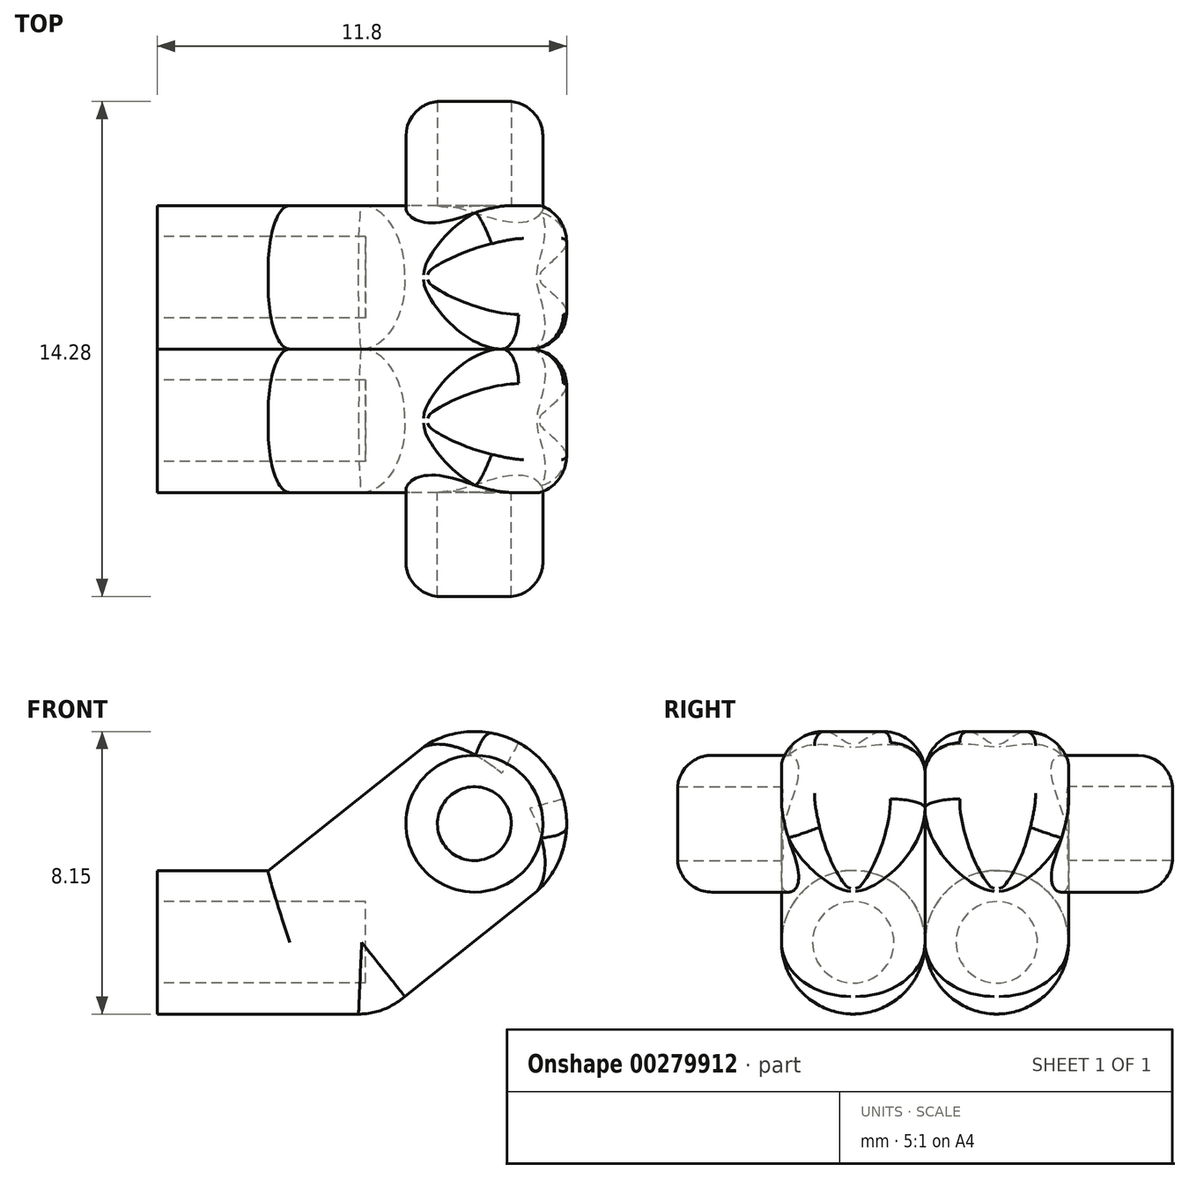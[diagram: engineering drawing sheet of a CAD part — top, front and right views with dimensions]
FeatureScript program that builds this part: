
annotation { "Feature Type Name" : "Feature", "Feature Type Description" : "" }
export const myFeature = defineFeature(function(context is Context, id is Id, definition is map)
    precondition{}
    {
        {
            var Q0;
            Q0=qCreatedBy(makeId("Right.planeOp"),FACE);
            var sketch = newSketch(context, id + "F0", { "sketchPlane" : qUnion([Q0])});
            skLineSegment(sketch, "E0.bottom", {"start": v(2.07, 2.07) * mm, "end": v(-2.07, 2.07) * mm});
            skLineSegment(sketch, "E0.top", {"start": v(2.07, -2.07) * mm, "end": v(-2.07, -2.07) * mm});
            skLineSegment(sketch, "E0.left", {"start": v(2.07, 2.07) * mm, "end": v(2.07, -2.07) * mm});
            skLineSegment(sketch, "E0.right", {"start": v(-2.07, 2.07) * mm, "end": v(-2.07, -2.07) * mm});
            skPoint(sketch, "E0.middle", {"position": v(0, 0) * mm});
            skCircle(sketch, "E1", {"center": v(0, 0) * mm, "radius": 2.07 * mm});
            skCircle(sketch, "E2", {"center": v(0, 0) * mm, "radius": 1.18 * mm});
            skSolve(sketch);
        }
        {
            var Q0;
            Q0 = qSketchRegion(id + "F0", true);
            var Q1;
            Q1=makeQuery(id+"F0.imprint","IMPRINT",FACE,{"disambiguationData":[TD([[makeQuery(id+"F0.imprint","IMPRINT",EDGE,{"derivedFrom":sQuery(id+"F0.wireOp",EDGE,"E2")}),1.0]])]});
            extrude(context, id + "F1", {"entities" : qUnion([Q0, Q1]), "depth" : 6.5 * mm});
        }
        {
            var Q0;
            Q0=makeQuery(id+"F1.opExtrude","SWEPT_FACE",FACE,{"disambiguationData":[OSD([sQuery(id+"F0.wireOp",EDGE,"E0.right")])]});
            var sketch = newSketch(context, id + "F2", { "sketchPlane" : qUnion([Q0])});
            skLineSegment(sketch, "E3", {"start": v(0, 2.07) * mm, "end": v(3.2, 2.07) * mm});
            skLineSegment(sketch, "E4", {"start": v(3.2, 2.07) * mm, "end": v(6.5, -2.07) * mm});
            skSolve(sketch);
        }
        {
            var Q0;
            {var subQ0=sQuery(id+"F2.wireOp",EDGE,"E4");Q0=makeQuery(id+"F2.imprint","IMPRINT",FACE,{"disambiguationData":[TD([[makeQuery(id+"F2.imprint","IMPRINT",EDGE,{"derivedFrom":subQ0}),1.0]])]});}
            extrude(context, id + "F3", {"entities" : qUnion([Q0]), "operationType" : NewBodyOperationType.REMOVE, "endBound" : BoundingType.THROUGH_ALL, "oppositeDirection" : true, "depth" : 25 * mm});
        }
        {
            var Q0;
            Q0=makeQuery(id+"F3.boolean.opBoolean","COPY",FACE,{"derivedFrom":makeQuery(id+"F3.opExtrude","SWEPT_FACE",FACE,{"disambiguationData":[OSD([sQuery(id+"F2.wireOp",EDGE,"E4")])]})});
            extrude(context, id + "F4", {"entities" : qUnion([Q0]), "operationType" : NewBodyOperationType.ADD, "depth" : 8.15 * mm});
        }
        {
            var Q0;
            {var subQ0=sQuery(id+"F0.wireOp",EDGE,"E0.right");var subQ1=sQuery(id+"F0.wireOp",EDGE,"E0.top");var subQ2=makeQuery(id+"F0.imprint","INTERSECT",VERTEX,{"derivedFrom":[subQ1,subQ0]});Q0=makeQuery(id+"F0.imprint","IMPRINT",FACE,{"disambiguationData":[TD([[makeQuery(id+"F0.imprint","IMPRINT",EDGE,{"disambiguationData":[TD([[subQ2,1.0]])],"derivedFrom":subQ1}),-1.0]])]});}
            var Q1;
            {var subQ0=sQuery(id+"F0.wireOp",EDGE,"E0.left");var subQ1=sQuery(id+"F0.wireOp",EDGE,"E0.top");var subQ2=makeQuery(id+"F0.imprint","INTERSECT",VERTEX,{"derivedFrom":[subQ1,subQ0]});Q1=makeQuery(id+"F0.imprint","IMPRINT",FACE,{"disambiguationData":[TD([[makeQuery(id+"F0.imprint","IMPRINT",EDGE,{"disambiguationData":[TD([[subQ2,-1.0]])],"derivedFrom":subQ1}),-1.0]])]});}
            extrude(context, id + "F5", {"entities" : qUnion([Q0, Q1]), "operationType" : NewBodyOperationType.REMOVE, "endBound" : BoundingType.THROUGH_ALL, "depth" : 25 * mm});
        }
        {
            var Q0;
            {var subQ0=sQuery(id+"F0.wireOp",EDGE,"E0.right");var subQ1=sQuery(id+"F0.wireOp",EDGE,"E0.bottom");var subQ2=makeQuery(id+"F0.imprint","INTERSECT",VERTEX,{"derivedFrom":[subQ1,subQ0]});Q0=makeQuery(id+"F0.imprint","IMPRINT",FACE,{"disambiguationData":[TD([[makeQuery(id+"F0.imprint","IMPRINT",EDGE,{"disambiguationData":[TD([[subQ2,1.0]])],"derivedFrom":subQ1}),1.0]])]});}
            var Q1;
            {var subQ0=sQuery(id+"F0.wireOp",EDGE,"E0.left");var subQ1=sQuery(id+"F0.wireOp",EDGE,"E0.bottom");var subQ2=makeQuery(id+"F0.imprint","INTERSECT",VERTEX,{"derivedFrom":[subQ1,subQ0]});Q1=makeQuery(id+"F0.imprint","IMPRINT",FACE,{"disambiguationData":[TD([[makeQuery(id+"F0.imprint","IMPRINT",EDGE,{"disambiguationData":[TD([[subQ2,-1.0]])],"derivedFrom":subQ1}),1.0]])]});}
            extrude(context, id + "F6", {"entities" : qUnion([Q0, Q1]), "operationType" : NewBodyOperationType.REMOVE, "depth" : 3.2 * mm});
        }
        {
            var Q0;
            Q0=makeQuery(id+"F4.boolean.opBoolean","MERGE",FACE,{"derivedFrom":[makeQuery(id+"F1.opExtrude","SWEPT_FACE",FACE,{"disambiguationData":[OSD([sQuery(id+"F0.wireOp",EDGE,"E0.right")])]}),makeQuery(id+"F4.opExtrude","SWEPT_FACE",FACE,{"disambiguationData":[OSD([sQuery(id+"F2.wireOp",EDGE,"E4")])]})]});
            var sketch = newSketch(context, id + "F7", { "sketchPlane" : qUnion([Q0])});
            skCircle(sketch, "E5", {"center": v(9.14, 3.42) * mm, "radius": 2.66 * mm});
            skPoint(sketch, "E5.first.point", {"position": v(11.22, 5.08) * mm});
            skPoint(sketch, "E5.second.point", {"position": v(7.73, 5.68) * mm});
            skPoint(sketch, "E5.third.point", {"position": v(10.98, 1.5) * mm});
            skCircle(sketch, "E6", {"center": v(9.14, 3.42) * mm, "radius": 1.98 * mm});
            skCircle(sketch, "E7", {"center": v(9.14, 3.42) * mm, "radius": 1.06 * mm});
            skSolve(sketch);
        }
        {
            var Q0;
            {var subQ0=sQuery(id+"F7.wireOp",EDGE,"E5");var subQ1=sQuery(id+"F2.wireOp",EDGE,"E4");var subQ4=makeQuery(id+"F4.opExtrude","CAP_EDGE",EDGE,{"disambiguationData":[OSD([subQ1])],"isStart":false});var subQ5=makeQuery(id+"F7.imprint","INTERSECT",VERTEX,{"derivedFrom":[subQ4,subQ0]});Q0=makeQuery(id+"F7.imprint","IMPRINT",FACE,{"disambiguationData":[TD([[makeQuery(id+"F7.imprint","IMPRINT",EDGE,{"disambiguationData":[TD([[subQ5,-1.0]])],"derivedFrom":subQ0}),-1.0]])]});}
            var Q1;
            {var subQ0=sQuery(id+"F7.wireOp",EDGE,"E5");var subQ1=sQuery(id+"F2.wireOp",EDGE,"E4");var subQ2=makeQuery(id+"F4.opExtrude","CAP_EDGE",EDGE,{"disambiguationData":[OSD([subQ1])],"isStart":false});var subQ3=makeQuery(id+"F7.imprint","INTERSECT",VERTEX,{"derivedFrom":[subQ2,subQ0]});Q1=makeQuery(id+"F7.imprint","IMPRINT",FACE,{"disambiguationData":[TD([[makeQuery(id+"F7.imprint","IMPRINT",EDGE,{"disambiguationData":[TD([[subQ3,1.0]])],"derivedFrom":subQ0}),-1.0]])]});}
            extrude(context, id + "F8", {"entities" : qUnion([Q0, Q1]), "operationType" : NewBodyOperationType.REMOVE, "endBound" : BoundingType.THROUGH_ALL, "oppositeDirection" : true, "depth" : 25 * mm});
        }
        {
            var Q0;
            Q0=makeQuery(id+"F4.opExtrude","SWEPT_EDGE",EDGE,{"disambiguationData":[OSD([sQuery(id+"F0.wireOp",EDGE,"E0.bottom"),sQuery(id+"F0.wireOp",EDGE,"E0.right"),sQuery(id+"F2.wireOp",EDGE,"E3"),sQuery(id+"F2.wireOp",EDGE,"E4")])]});
            var Q1;
            Q1=makeQuery(id+"F4.opExtrude","SWEPT_EDGE",EDGE,{"disambiguationData":[OSD([sQuery(id+"F0.wireOp",EDGE,"E0.left"),sQuery(id+"F2.wireOp",EDGE,"E4")])]});
            var Q2;
            Q2=makeQuery(id+"F4.opExtrude","SWEPT_EDGE",EDGE,{"disambiguationData":[OSD([sQuery(id+"F0.wireOp",EDGE,"E0.top"),sQuery(id+"F0.wireOp",EDGE,"E0.right"),sQuery(id+"F2.wireOp",EDGE,"E4")])]});
            fillet(context, id + "F9", {"entities" : qUnion([Q0, Q1, Q2]), "radius" : 2 * mm, "tangentPropagation" : true, "allowEdgeOverflow" : false});
        }
        {
            var Q0;
            Q0=makeQuery(id+"F7.imprint","IMPRINT",FACE,{"disambiguationData":[TD([[makeQuery(id+"F7.imprint","IMPRINT",EDGE,{"derivedFrom":sQuery(id+"F7.wireOp",EDGE,"E6")}),1.0]])]});
            extrude(context, id + "F10", {"entities" : qUnion([Q0]), "operationType" : NewBodyOperationType.ADD, "depth" : 3 * mm, "hasSecondDirection" : true, "secondDirectionOppositeDirection" : true, "secondDirectionDepth" : 1 * mm});
        }
        {
            var Q0;
            {var subQ0=sQuery(id+"F7.wireOp",EDGE,"E5");var subQ1=sQuery(id+"F2.wireOp",EDGE,"E4");var subQ2=makeQuery(id+"F7.imprint","INTERSECT",VERTEX,{"derivedFrom":[makeQuery(id+"F4.opExtrude","CAP_EDGE",EDGE,{"disambiguationData":[OSD([subQ1])],"isStart":false}),subQ0]});var subQ3=sQuery(id+"F0.wireOp",EDGE,"E0.right");var subQ4=makeQuery(id+"F4.opExtrude","SWEPT_EDGE",EDGE,{"disambiguationData":[OSD([sQuery(id+"F0.wireOp",EDGE,"E0.bottom"),subQ3,sQuery(id+"F2.wireOp",EDGE,"E3"),subQ1])]});Q0=makeQuery(id+"F9.opFillet","BLEND_EDGE",EDGE,{"blendedFrom":[subQ4,makeQuery(id+"F8.boolean.opBoolean","TWEAK_FACE",FACE,{"derivedFrom":[makeQuery(id+"F8.opExtrude","SWEPT_FACE",FACE,{"disambiguationData":[OSD([subQ0]),TDD([makeQuery(id+"F7.imprint","IMPRINT",EDGE,{"disambiguationData":[TD([[subQ2,-1.0]])],"derivedFrom":subQ0})])]}),makeQuery(id+"F8.opExtrude","SWEPT_FACE",FACE,{"disambiguationData":[OSD([subQ0]),TDD([makeQuery(id+"F7.imprint","IMPRINT",EDGE,{"disambiguationData":[TD([[subQ2,1.0]])],"derivedFrom":subQ0})])]})]})],"blendedInto":[makeQuery(id+"F8.boolean.opBoolean","TWEAK_FACE",FACE,{"derivedFrom":[makeQuery(id+"F8.opExtrude","SWEPT_FACE",FACE,{"disambiguationData":[OSD([subQ0]),TDD([makeQuery(id+"F7.imprint","IMPRINT",EDGE,{"disambiguationData":[TD([[subQ2,-1.0]])],"derivedFrom":subQ0})])]}),makeQuery(id+"F8.opExtrude","SWEPT_FACE",FACE,{"disambiguationData":[OSD([subQ0]),TDD([makeQuery(id+"F7.imprint","IMPRINT",EDGE,{"disambiguationData":[TD([[subQ2,1.0]])],"derivedFrom":subQ0})])]})]})]});}
            var Q1;
            {var subQ0=sQuery(id+"F7.wireOp",EDGE,"E5");var subQ1=sQuery(id+"F2.wireOp",EDGE,"E4");var subQ2=makeQuery(id+"F7.imprint","INTERSECT",VERTEX,{"derivedFrom":[makeQuery(id+"F4.opExtrude","CAP_EDGE",EDGE,{"disambiguationData":[OSD([subQ1])],"isStart":false}),subQ0]});Q1=makeQuery(id+"F8.boolean.opBoolean","TWEAK_EDGE",EDGE,{"derivedFrom":[makeQuery(id+"F8.opExtrude","CAP_EDGE",EDGE,{"disambiguationData":[OSD([subQ0]),TDD([makeQuery(id+"F7.imprint","IMPRINT",EDGE,{"disambiguationData":[TD([[subQ2,-1.0]])],"derivedFrom":subQ0})])],"isStart":true}),makeQuery(id+"F8.opExtrude","CAP_EDGE",EDGE,{"disambiguationData":[OSD([subQ0]),TDD([makeQuery(id+"F7.imprint","IMPRINT",EDGE,{"disambiguationData":[TD([[subQ2,1.0]])],"derivedFrom":subQ0})])],"isStart":true})]});}
            var Q2;
            {var subQ0=sQuery(id+"F7.wireOp",EDGE,"E5");var subQ1=sQuery(id+"F2.wireOp",EDGE,"E4");var subQ2=makeQuery(id+"F7.imprint","INTERSECT",VERTEX,{"derivedFrom":[makeQuery(id+"F4.opExtrude","CAP_EDGE",EDGE,{"disambiguationData":[OSD([subQ1])],"isStart":false}),subQ0]});var subQ4=sQuery(id+"F0.wireOp",EDGE,"E0.top");Q2=makeQuery(id+"F9.opFillet","BLEND_EDGE",EDGE,{"blendedFrom":[makeQuery(id+"F4.opExtrude","SWEPT_EDGE",EDGE,{"disambiguationData":[OSD([subQ4,sQuery(id+"F0.wireOp",EDGE,"E0.left")])]}),makeQuery(id+"F8.boolean.opBoolean","TWEAK_FACE",FACE,{"derivedFrom":[makeQuery(id+"F8.opExtrude","SWEPT_FACE",FACE,{"disambiguationData":[OSD([subQ0]),TDD([makeQuery(id+"F7.imprint","IMPRINT",EDGE,{"disambiguationData":[TD([[subQ2,-1.0]])],"derivedFrom":subQ0})])]}),makeQuery(id+"F8.opExtrude","SWEPT_FACE",FACE,{"disambiguationData":[OSD([subQ0]),TDD([makeQuery(id+"F7.imprint","IMPRINT",EDGE,{"disambiguationData":[TD([[subQ2,1.0]])],"derivedFrom":subQ0})])]})]})],"blendedInto":[makeQuery(id+"F8.boolean.opBoolean","TWEAK_FACE",FACE,{"derivedFrom":[makeQuery(id+"F8.opExtrude","SWEPT_FACE",FACE,{"disambiguationData":[OSD([subQ0]),TDD([makeQuery(id+"F7.imprint","IMPRINT",EDGE,{"disambiguationData":[TD([[subQ2,-1.0]])],"derivedFrom":subQ0})])]}),makeQuery(id+"F8.opExtrude","SWEPT_FACE",FACE,{"disambiguationData":[OSD([subQ0]),TDD([makeQuery(id+"F7.imprint","IMPRINT",EDGE,{"disambiguationData":[TD([[subQ2,1.0]])],"derivedFrom":subQ0})])]})]})]});}
            var Q3;
            {var subQ0=sQuery(id+"F7.wireOp",EDGE,"E5");var subQ1=sQuery(id+"F2.wireOp",EDGE,"E4");var subQ2=makeQuery(id+"F7.imprint","INTERSECT",VERTEX,{"derivedFrom":[makeQuery(id+"F4.opExtrude","CAP_EDGE",EDGE,{"disambiguationData":[OSD([subQ1])],"isStart":false}),subQ0]});Q3=makeQuery(id+"F9.opFillet","BLEND_EDGE",EDGE,{"blendedFrom":[makeQuery(id+"F4.opExtrude","SWEPT_EDGE",EDGE,{"disambiguationData":[OSD([sQuery(id+"F0.wireOp",EDGE,"E0.left"),subQ1])]}),makeQuery(id+"F8.boolean.opBoolean","TWEAK_FACE",FACE,{"derivedFrom":[makeQuery(id+"F8.opExtrude","SWEPT_FACE",FACE,{"disambiguationData":[OSD([subQ0]),TDD([makeQuery(id+"F7.imprint","IMPRINT",EDGE,{"disambiguationData":[TD([[subQ2,-1.0]])],"derivedFrom":subQ0})])]}),makeQuery(id+"F8.opExtrude","SWEPT_FACE",FACE,{"disambiguationData":[OSD([subQ0]),TDD([makeQuery(id+"F7.imprint","IMPRINT",EDGE,{"disambiguationData":[TD([[subQ2,1.0]])],"derivedFrom":subQ0})])]})]})],"blendedInto":[makeQuery(id+"F8.boolean.opBoolean","TWEAK_FACE",FACE,{"derivedFrom":[makeQuery(id+"F8.opExtrude","SWEPT_FACE",FACE,{"disambiguationData":[OSD([subQ0]),TDD([makeQuery(id+"F7.imprint","IMPRINT",EDGE,{"disambiguationData":[TD([[subQ2,-1.0]])],"derivedFrom":subQ0})])]}),makeQuery(id+"F8.opExtrude","SWEPT_FACE",FACE,{"disambiguationData":[OSD([subQ0]),TDD([makeQuery(id+"F7.imprint","IMPRINT",EDGE,{"disambiguationData":[TD([[subQ2,1.0]])],"derivedFrom":subQ0})])]})]})]});}
            var Q4;
            {var subQ0=sQuery(id+"F7.wireOp",EDGE,"E5");var subQ1=sQuery(id+"F2.wireOp",EDGE,"E4");var subQ2=makeQuery(id+"F7.imprint","INTERSECT",VERTEX,{"derivedFrom":[makeQuery(id+"F4.opExtrude","CAP_EDGE",EDGE,{"disambiguationData":[OSD([subQ1])],"isStart":false}),subQ0]});var subQ4=sQuery(id+"F0.wireOp",EDGE,"E0.left");Q4=makeQuery(id+"F8.boolean.opBoolean","INTERSECT",EDGE,{"derivedFrom":[makeQuery(id+"F4.boolean.opBoolean","MERGE",FACE,{"derivedFrom":[makeQuery(id+"F1.opExtrude","SWEPT_FACE",FACE,{"disambiguationData":[OSD([subQ4])]}),makeQuery(id+"F4.opExtrude","SWEPT_FACE",FACE,{"disambiguationData":[OSD([subQ4,subQ1])]})]}),makeQuery(id+"F8.opExtrude","SWEPT_FACE",FACE,{"disambiguationData":[OSD([subQ0]),TDD([makeQuery(id+"F7.imprint","IMPRINT",EDGE,{"disambiguationData":[TD([[subQ2,-1.0]])],"derivedFrom":subQ0})])]}),makeQuery(id+"F8.opExtrude","SWEPT_FACE",FACE,{"disambiguationData":[OSD([subQ0]),TDD([makeQuery(id+"F7.imprint","IMPRINT",EDGE,{"disambiguationData":[TD([[subQ2,1.0]])],"derivedFrom":subQ0})])]})]});}
            var Q5;
            {var subQ0=sQuery(id+"F7.wireOp",EDGE,"E5");var subQ1=sQuery(id+"F2.wireOp",EDGE,"E4");var subQ2=makeQuery(id+"F7.imprint","INTERSECT",VERTEX,{"derivedFrom":[makeQuery(id+"F4.opExtrude","CAP_EDGE",EDGE,{"disambiguationData":[OSD([subQ1])],"isStart":false}),subQ0]});var subQ3=sQuery(id+"F0.wireOp",EDGE,"E0.right");var subQ4=makeQuery(id+"F4.opExtrude","SWEPT_EDGE",EDGE,{"disambiguationData":[OSD([sQuery(id+"F0.wireOp",EDGE,"E0.top"),subQ3,subQ1])]});Q5=makeQuery(id+"F9.opFillet","BLEND_EDGE",EDGE,{"blendedFrom":[subQ4,makeQuery(id+"F8.boolean.opBoolean","TWEAK_FACE",FACE,{"derivedFrom":[makeQuery(id+"F8.opExtrude","SWEPT_FACE",FACE,{"disambiguationData":[OSD([subQ0]),TDD([makeQuery(id+"F7.imprint","IMPRINT",EDGE,{"disambiguationData":[TD([[subQ2,-1.0]])],"derivedFrom":subQ0})])]}),makeQuery(id+"F8.opExtrude","SWEPT_FACE",FACE,{"disambiguationData":[OSD([subQ0]),TDD([makeQuery(id+"F7.imprint","IMPRINT",EDGE,{"disambiguationData":[TD([[subQ2,1.0]])],"derivedFrom":subQ0})])]})]})],"blendedInto":[makeQuery(id+"F8.boolean.opBoolean","TWEAK_FACE",FACE,{"derivedFrom":[makeQuery(id+"F8.opExtrude","SWEPT_FACE",FACE,{"disambiguationData":[OSD([subQ0]),TDD([makeQuery(id+"F7.imprint","IMPRINT",EDGE,{"disambiguationData":[TD([[subQ2,-1.0]])],"derivedFrom":subQ0})])]}),makeQuery(id+"F8.opExtrude","SWEPT_FACE",FACE,{"disambiguationData":[OSD([subQ0]),TDD([makeQuery(id+"F7.imprint","IMPRINT",EDGE,{"disambiguationData":[TD([[subQ2,1.0]])],"derivedFrom":subQ0})])]})]})]});}
            fillet(context, id + "F11", {"entities" : qUnion([Q0, Q1, Q2, Q3, Q4, Q5]), "radius" : 1 * mm, "tangentPropagation" : true, "allowEdgeOverflow" : false});
        }
        {
            var Q0;
            Q0=makeQuery(id+"F10.opExtrude","CAP_EDGE",EDGE,{"disambiguationData":[OSD([sQuery(id+"F7.wireOp",EDGE,"E6")])],"isStart":false});
            fillet(context, id + "F12", {"entities" : qUnion([Q0]), "radius" : 1 * mm, "tangentPropagation" : true, "allowEdgeOverflow" : false});
        }
        {
            var Q0;
            Q0=makeQuery(id+"F0.imprint","IMPRINT",FACE,{"disambiguationData":[TD([[makeQuery(id+"F0.imprint","IMPRINT",EDGE,{"derivedFrom":sQuery(id+"F0.wireOp",EDGE,"E2")}),1.0]])]});
            extrude(context, id + "F13", {"entities" : qUnion([Q0]), "operationType" : NewBodyOperationType.REMOVE, "depth" : 6 * mm});
        }
        {
            var Q0;
            Q0=makeQuery(id+"F1.opExtrude","SWEPT_BODY",BODY,{"disambiguationData":[OSD([sQuery(id+"F0.wireOp",EDGE,"E0.bottom"),sQuery(id+"F0.wireOp",EDGE,"E0.top"),sQuery(id+"F0.wireOp",EDGE,"E0.left"),sQuery(id+"F0.wireOp",EDGE,"E0.right")])]});
            var Q1;
            {var subQ0=sQuery(id+"F0.wireOp",EDGE,"E0.left");Q1=makeQuery(id+"F4.boolean.opBoolean","MERGE",FACE,{"derivedFrom":[makeQuery(id+"F1.opExtrude","SWEPT_FACE",FACE,{"disambiguationData":[OSD([subQ0])]}),makeQuery(id+"F4.opExtrude","SWEPT_FACE",FACE,{"disambiguationData":[OSD([subQ0,sQuery(id+"F2.wireOp",EDGE,"E4")])]})]});}
            mirror(context, id + "F14", {"entities" : qUnion([Q0]), "mirrorPlane" : qUnion([Q1])});
        }
    });
